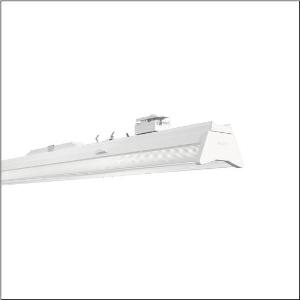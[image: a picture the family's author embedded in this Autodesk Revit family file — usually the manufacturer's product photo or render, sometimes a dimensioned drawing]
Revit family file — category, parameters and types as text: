
# Revit family: licross_r__21_performance_ho_52tm16mn4e5m_7be5
name_source: partatom
category: Lighting Fixtures
units: mm (PartAtom-declared; Revit-internal decimal feet)

## family parameters
Cut with Voids When Loaded = No
Host = Face
Light Source = No
Part Type = Normal
Room Calculation Point = No
Round Connector Dimension = Use Diameter
Shared = No

## types (1)
- --- (1 x LED, 14970 lm, 83.2 W, 4000K)
    Apparent Load = 83 VA
    CIE Flux Codes = 63 87 95 78 100
    Color Rendering = 80
    Color Temperature = 4000K
    Default Elevation = 1800 mm
    Description = Licross® 21 Performance HO, luminaire insert, of sheet steel, galvanised, coil coated, white, length: 1.500mm, width: 120mm, height: 123mm, LED rated luminous flux: 14.970lm, light colour: 840, control gear: ON/OFF Multilumen, with plug, 3-pole, with phase selection, mains connection: 220..240V, AC, 50/60Hz, rated input power: 83W, halogen-free wiring, primary light control with lens, of plastic, primary optical cover: cover, of PMMA, light emission: direct/indirect distribution, primary light characteristic: symmetric, protection rating (complete): IP40, insulation class (complete): insulation class I (protective earthing), certification: CE, ENEC, UKCA, protection symbol: D if used in an environment without relevant dust loads with corresponding accessories, impact resistance: IK06, permissible ambient temperature for indoor applications: -35..+35°C, corresponds to IFS (International Featured Standards) requirements for safety and quality in the food industry, reducing of maximum allowable ambient temperature of 5°C with ceiling mounting, LABS conformity tested according to VDMA 24364:2018-05, packaging unit: 1 piece
    Height = 114 mm
    Lamp = 1 x LED
    Lamp Light Flux = 14970 lm
    Lamp Power = 83.2 W
    Lamp count = 1
    Length = 1500 mm
    Luminous efficacy = 180 lm/W
    Manufacturer = Siteco
    ModVariant = No
    Model = 52TM16MN4E5M
    Mounting Place = Ceiling
    Mounting Type = Pendant
    Number of Poles = 1
    OnlyDefault = Yes
    Power Factor = 1
    Product Name = Licross® 21 Performance HO
    Product group = luminaire insert
    ProductGroupID = 901
    Protection Class = Protection class I
    Protection Degree = IP 40
    RLX_Detail_Level = 1
    RLX_Emergency_Light_Flux = 0 lm
    RLX_Emergency_Type = 0
    RLX_Emergency_Type_DB = No
    RlxData = <blob elided: 31761 chars, md5=b58918dc>
    Socket = socket
    Standby Power = 0 W
    System Light Flux = 14970 lm
    System Power = 83 W
    Type Comments = factory setting: luminous flux: 100 % | (A | C | E) | 195 mA
    Type Image = l_1256138.jpg
    URL = http://relux.com
    VarID = @adj_057541
    Voltage = 0 V
    Weight = 0.00 kg
    Width = 120 mm

## geometry (parser evidence)
native form markers: Blend x4, Sweep x12
no freeform markers — native parametric forms only
